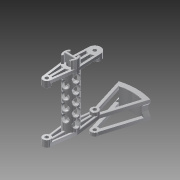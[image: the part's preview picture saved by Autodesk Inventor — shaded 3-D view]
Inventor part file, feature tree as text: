
AUTODESK INVENTOR PART (.ipt)
format: ipt  version: 2014 (Build 180170000, 170)  size: 1,106,432 bytes
history: native  units: mm
features: extrude x12, sketch x7, fillet x3, plane x1, chamfer x1
ambient origin geometry x8: Origin, YZ Plane, XZ Plane, XY Plane, X Axis, Y Axis, Z Axis, Center Point
bodies: Solid1 (feature_tree)
feature tree (24):
  sketch  "Sketch1"  dims[d2=4.0mm d3=6.35mm]
  extrude  "Extrusion1"  Depth=6.35mm
  extrude  "Extrusion2"  Depth=4.0mm
  extrude  "Extrusion3"  Depth=4.0mm
  plane  "Work Plane1"
  extrude  "Extrusion4"  Depth=2.0mm
  extrude  "Extrusion5"  Depth=2.0mm
  extrude  "Extrusion6"  Depth=45.0mm
  extrude  "Extrusion7"  Depth=2.0mm
  extrude  "Extrusion8"  Depth=2.0mm
  extrude  "Extrusion9"  Depth=2.0mm
  extrude  "Extrusion10"  Depth=2.0mm
  fillet  "Fillet1"  Radius=45.0mm
  fillet  "Fillet2"  Radius=6.0mm
  extrude  "Extrusion11"  Depth=2.0mm TaperAngle=0.0deg
  fillet  "Fillet3"  [1 undecoded]
  extrude  "Extrusion12"  Depth=2.0mm
  chamfer  "Chamfer1"  Distance=10.0mm
  sketch  "Sketch7"  dims[d14=6.5mm d15=45.0mm]
  sketch  "Sketch8"  dims[d16=6.35mm d17=4.0mm d18=4.0mm d19=2.0mm d20=2.0mm d21=45.0mm d22=6.0mm d23=0.0mm d24=12.0mm d25=0.0mm d27=0.0mm d28=108.0mm d31=10.0mm d34=5.0mm d35=5.0mm d36=5.0mm d37=5.0mm d38=10.0mm d39=45.0deg d40=4.0mm d41=4.0mm d42=4.0mm d43=2.0mm d44=4.0mm d45=6.0mm d46=0.0mm d47=12.0mm d48=0.0mm d49=6.0mm d50=6.0mm d51=30.0mm d52=30.0mm d53=10.0mm d54=62.0mm d55=6.0mm d56=0.0mm d57=27.0mm d58=0.0mm d59=21.0mm d60=0.0mm d62=6.0mm d63=0.0mm d64=14.0mm d65=30.0mm d66=0.0mm d70=14.0mm d71=14.0mm d72=14.0mm d73=14.0mm d74=4.333333mm d75=4.333333mm d76=4.333333mm d77=4.333333mm d78=4.333333mm d79=4.333333mm d80=13.0mm d81=13.0mm d82=13.0mm d83=13.0mm d84=13.0mm d85=13.0mm d86=14.0mm d87=4.333333mm d88=14.0mm d89=14.0mm d90=14.0mm d91=4.333333mm d92=4.333333mm d93=26.5mm d94=26.5mm d95=30.0mm d96=0.0mm d97=1.0mm d98=1.0mm d99=4.0mm d100=2.0mm d101=2.0mm d102=45.0deg d103=45.0deg d104=15.0mm d105=0.0mm d106=1.0mm d107=32.0mm d108=26.0mm d109=7.5mm d110=8.774964mm d111=8.774964mm d112=4.0mm d113=10.0mm d114=0.0mm d115=90.0mm d116=6.0mm d117=2.0mm d118=45.0deg d119=150.0mm]
  sketch  "Sketch3"  dims[d5=13.0mm d7=4.0mm]
  sketch  "Sketch4"  dims[d8=4.0mm d9=4.0mm]
  sketch  "Sketch5"  dims[d10=4.0mm d11=2.0mm]
  sketch  "Sketch6"  dims[d12=2.0mm d13=4.0mm]
note: 1 required parameter value undecoded (feature->parameter linkage not recoverable at this tier; creation-order binding heuristic only, values carry confidence <= 0.55)
